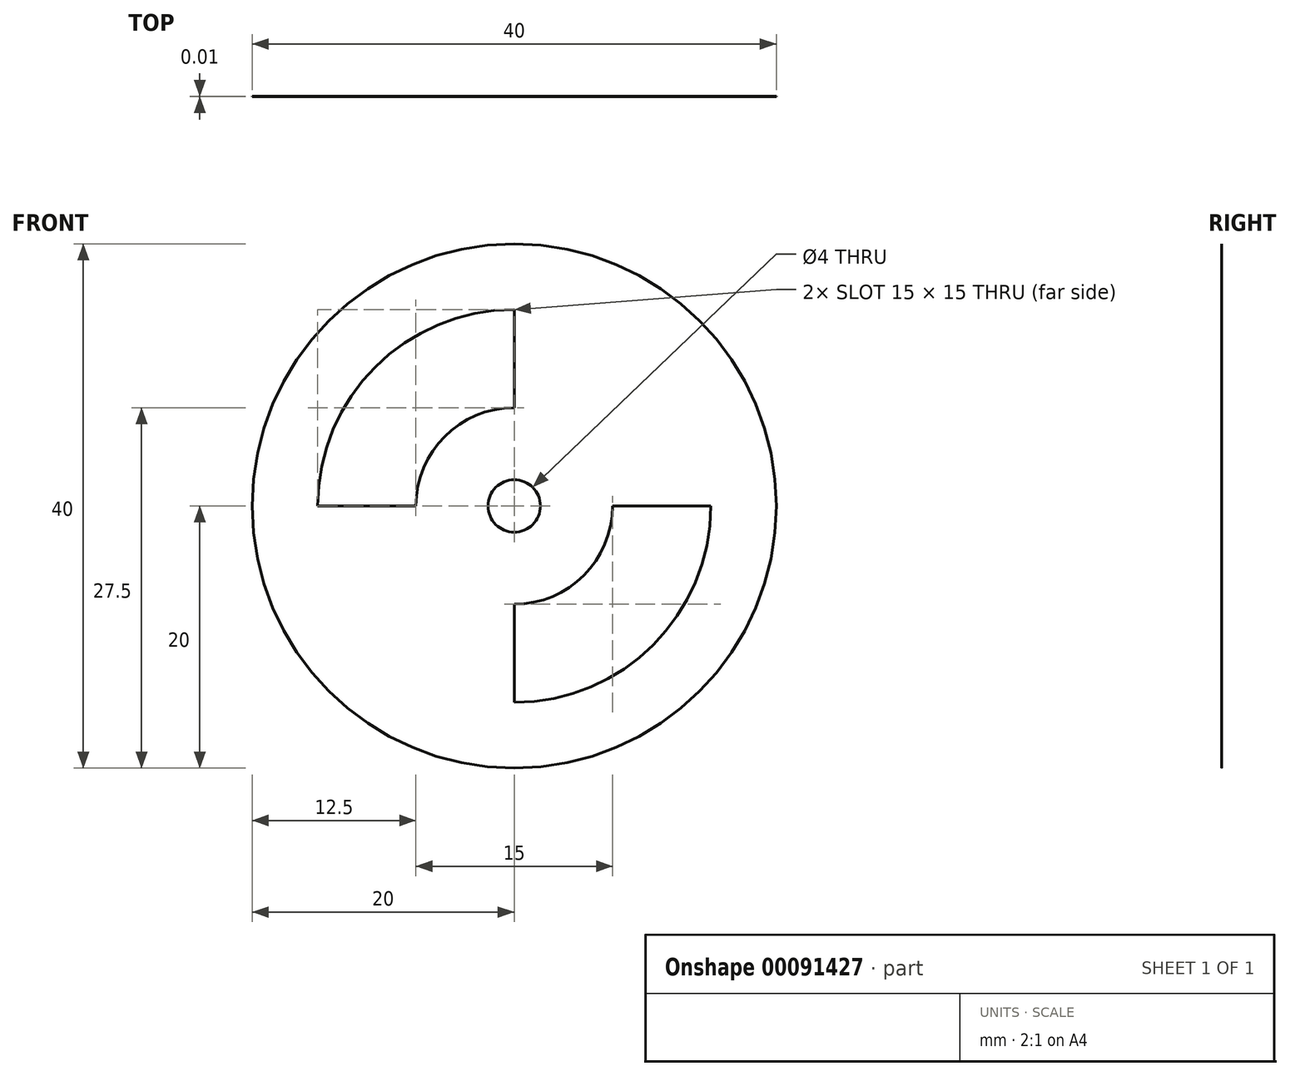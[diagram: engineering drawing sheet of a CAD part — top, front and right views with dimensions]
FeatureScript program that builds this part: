
annotation { "Feature Type Name" : "Feature", "Feature Type Description" : "" }
export const myFeature = defineFeature(function(context is Context, id is Id, definition is map)
    precondition{}
    {
        {
            var Q0;
            Q0=qCreatedBy(makeId("Front.planeOp"),FACE);
            var sketch = newSketch(context, id + "F0", { "sketchPlane" : qUnion([Q0])});
            skCircle(sketch, "E0", {"center": v(0, 0) * mm, "radius": 20 * mm});
            skCircle(sketch, "E1", {"center": v(0, 0) * mm, "radius": 2 * mm});
            skCircle(sketch, "E2", {"center": v(0, 0) * mm, "radius": 15 * mm});
            skCircle(sketch, "E3", {"center": v(0, 0) * mm, "radius": 7.5 * mm});
            skLineSegment(sketch, "E4", {"start": v(0, 15) * mm, "end": v(0, 7.5) * mm});
            skLineSegment(sketch, "E5", {"start": v(-7.5, 0) * mm, "end": v(-15, 0) * mm});
            skLineSegment(sketch, "E6", {"start": v(0, -7.5) * mm, "end": v(0, -15) * mm});
            skLineSegment(sketch, "E7", {"start": v(7.5, 0) * mm, "end": v(15, 0) * mm});
            skSolve(sketch);
        }
        {
            var Q0;
            Q0 = qSketchRegion(id + "F0", true);
            var Q1;
            Q1=makeQuery(id+"F0.imprint","IMPRINT",FACE,{"disambiguationData":[TD([[makeQuery(id+"F0.imprint","IMPRINT",EDGE,{"derivedFrom":sQuery(id+"F0.wireOp",EDGE,"E1")}),-1.0]])]});
            var Q2;
            {var subQ0=sQuery(id+"F0.wireOp",EDGE,"E5");Q2=makeQuery(id+"F0.imprint","IMPRINT",FACE,{"disambiguationData":[TD([[makeQuery(id+"F0.imprint","IMPRINT",EDGE,{"derivedFrom":subQ0}),1.0]])]});}
            var Q3;
            {var subQ0=sQuery(id+"F0.wireOp",EDGE,"E4");Q3=makeQuery(id+"F0.imprint","IMPRINT",FACE,{"disambiguationData":[TD([[makeQuery(id+"F0.imprint","IMPRINT",EDGE,{"derivedFrom":subQ0}),1.0]])]});}
            extrude(context, id + "F1", {"entities" : qUnion([Q0, Q1, Q2, Q3]), "depth" : 1 / 101.6 * mm});
        }
    });
